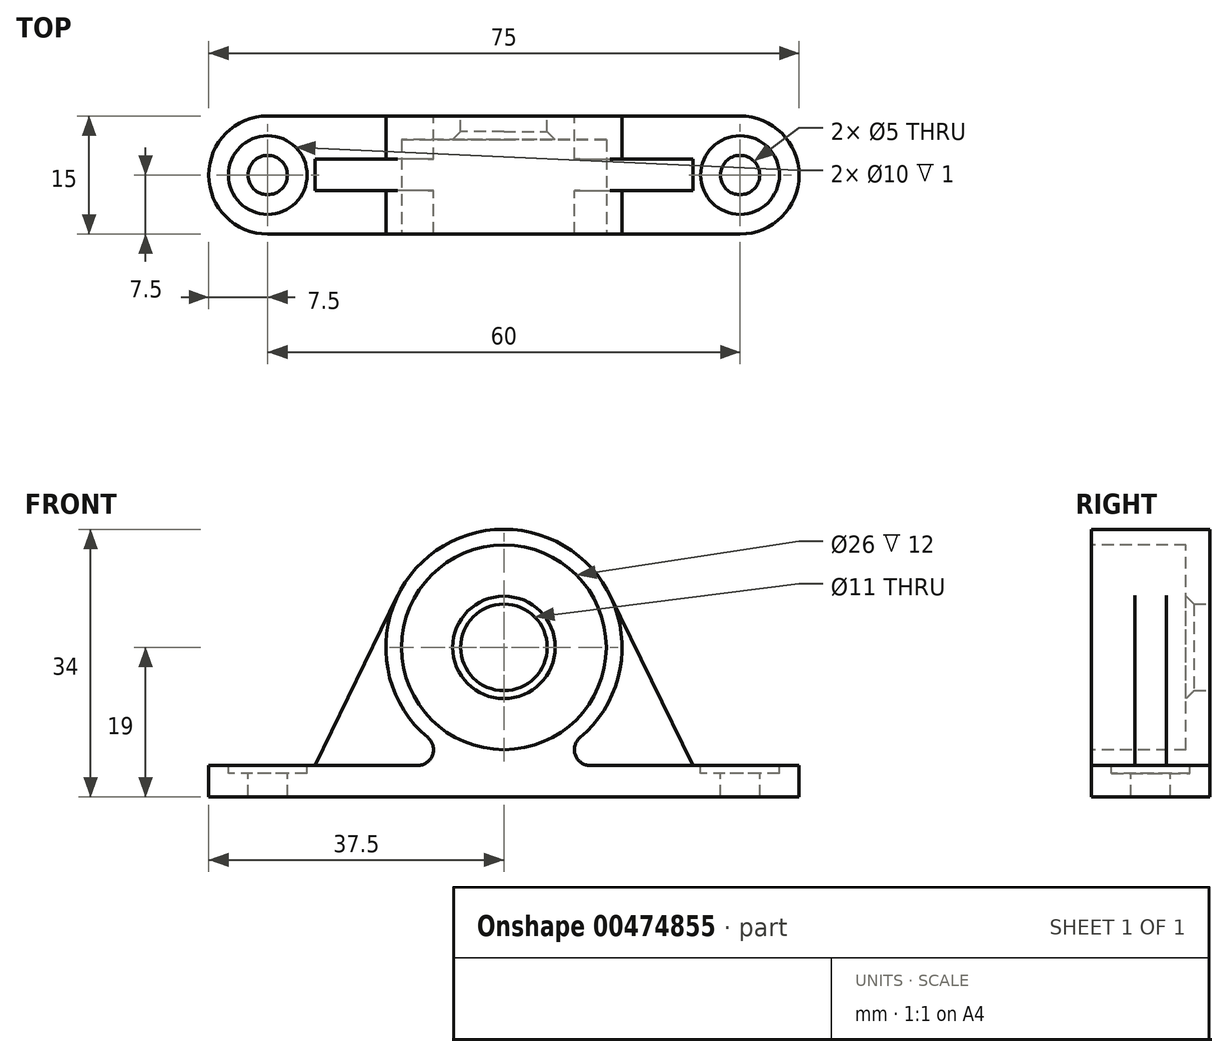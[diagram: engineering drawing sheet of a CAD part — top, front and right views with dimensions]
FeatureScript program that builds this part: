
annotation { "Feature Type Name" : "Feature", "Feature Type Description" : "" }
export const myFeature = defineFeature(function(context is Context, id is Id, definition is map)
    precondition{}
    {
        {
            assignVariable(context, id + "F0", {"name" : "Thickness", "anyValue" : 15});
        }
        {
            var Q0;
            Q0=qCreatedBy(makeId("Front.planeOp"),FACE);
            var sketch = newSketch(context, id + "F1", { "sketchPlane" : qUnion([Q0])});
            skLineSegment(sketch, "E0", {"start": v(0, 0) * mm, "end": v(-37.5, 0) * mm});
            skLineSegment(sketch, "E1", {"start": v(-37.5, 0) * mm, "end": v(-37.5, 4) * mm});
            skLineSegment(sketch, "E2", {"start": v(-37.5, 4) * mm, "end": v(-10.95, 4) * mm});
            skLineSegment(sketch, "E3", {"start": v(0, -14.72) * mm, "end": v(0, 62.74) * mm, "construction": true});
            skArc(sketch, "E4", {"start": v(-9.67, 7.53) * mm, "mid": v(-14.1, 24.14) * mm, "end": v(0, 34) * mm});
            skPoint(sketch, "E5.visualSharp", {"position": v(0, 4) * mm});
            skArc(sketch, "E5.filletArc", {"start": v(-10.95, 4) * mm, "mid": v(-9.08, 5.31) * mm, "end": v(-9.67, 7.53) * mm});
            skLineSegment(sketch, "E6.MirrorCS", {"start": v(37.5, 0) * mm, "end": v(37.5, 4) * mm});
            skLineSegment(sketch, "E7.MirrorCS", {"start": v(37.5, 4) * mm, "end": v(10.95, 4) * mm});
            skLineSegment(sketch, "E8.MirrorCS", {"start": v(0, 0) * mm, "end": v(37.5, 0) * mm});
            skArc(sketch, "E9.MirrorCS", {"start": v(9.67, 7.53) * mm, "mid": v(14.1, 24.14) * mm, "end": v(0, 34) * mm});
            skArc(sketch, "E10.MirrorCS", {"start": v(10.95, 4) * mm, "mid": v(9.08, 5.31) * mm, "end": v(9.67, 7.53) * mm});
            skArc(sketch, "E11", {"start": v(-9.67, 7.53) * mm, "mid": v(0, 4) * mm, "end": v(9.67, 7.53) * mm, "construction": true});
            skSolve(sketch);
        }
        {
            var Q0;
            Q0=qSketchRegion(id+"F1",true);
            extrude(context, id + "F2", {"entities" : qUnion([Q0]), "endBound" : BoundingType.SYMMETRIC, "depth" : 15 * mm});
        }
        {
            var Q0;
            Q0=makeQuery(id+"F2.opExtrude","CAP_FACE",FACE,{"disambiguationData":[OSD([sQuery(id+"F1.wireOp",EDGE,"E0"),sQuery(id+"F1.wireOp",EDGE,"E1"),sQuery(id+"F1.wireOp",EDGE,"E2"),sQuery(id+"F1.wireOp",EDGE,"E5.filletArc"),sQuery(id+"F1.wireOp",EDGE,"E6.MirrorCS"),sQuery(id+"F1.wireOp",EDGE,"E7.MirrorCS"),sQuery(id+"F1.wireOp",EDGE,"E8.MirrorCS"),sQuery(id+"F1.wireOp",EDGE,"E9.MirrorCS"),sQuery(id+"F1.wireOp",EDGE,"E10.MirrorCS"),sQuery(id+"F1.wireOp",EDGE,"E4")])],"isStart":false});
            var sketch = newSketch(context, id + "F3", { "sketchPlane" : qUnion([Q0])});
            skCircle(sketch, "E12", {"center": v(0, 19) * mm, "radius": 13 * mm});
            skSolve(sketch);
        }
        {
            var Q0;
            Q0 = qSketchRegion(id + "F3", true);
            extrude(context, id + "F4", {"entities" : qUnion([Q0]), "operationType" : NewBodyOperationType.REMOVE, "oppositeDirection" : true, "depth" : (getVariable(context, 'Thickness') - 3) * mm});
        }
        {
            var Q0;
            Q0=makeQuery(id+"F2.opExtrude","CAP_FACE",FACE,{"disambiguationData":[OSD([sQuery(id+"F1.wireOp",EDGE,"E0"),sQuery(id+"F1.wireOp",EDGE,"E1"),sQuery(id+"F1.wireOp",EDGE,"E2"),sQuery(id+"F1.wireOp",EDGE,"E5.filletArc"),sQuery(id+"F1.wireOp",EDGE,"E6.MirrorCS"),sQuery(id+"F1.wireOp",EDGE,"E7.MirrorCS"),sQuery(id+"F1.wireOp",EDGE,"E8.MirrorCS"),sQuery(id+"F1.wireOp",EDGE,"E9.MirrorCS"),sQuery(id+"F1.wireOp",EDGE,"E10.MirrorCS"),sQuery(id+"F1.wireOp",EDGE,"E4")])],"isStart":true});
            var sketch = newSketch(context, id + "F5", { "sketchPlane" : qUnion([Q0])});
            skCircle(sketch, "E13", {"center": v(0, 19) * mm, "radius": 5.5 * mm});
            skSolve(sketch);
        }
        {
            var Q0;
            Q0 = qSketchRegion(id + "F5", true);
            extrude(context, id + "F6", {"entities" : qUnion([Q0]), "operationType" : NewBodyOperationType.REMOVE, "endBound" : BoundingType.THROUGH_ALL, "oppositeDirection" : true, "depth" : 25 * mm});
        }
        {
            var Q0;
            Q0=makeQuery(id+"F2.opExtrude","CAP_EDGE",EDGE,{"disambiguationData":[OSD([sQuery(id+"F1.wireOp",EDGE,"E6.MirrorCS")])],"isStart":false});
            var Q1;
            Q1=makeQuery(id+"F2.opExtrude","CAP_EDGE",EDGE,{"disambiguationData":[OSD([sQuery(id+"F1.wireOp",EDGE,"E6.MirrorCS")])],"isStart":true});
            var Q2;
            Q2=makeQuery(id+"F2.opExtrude","CAP_EDGE",EDGE,{"disambiguationData":[OSD([sQuery(id+"F1.wireOp",EDGE,"E1")])],"isStart":false});
            var Q3;
            Q3=makeQuery(id+"F2.opExtrude","CAP_EDGE",EDGE,{"disambiguationData":[OSD([sQuery(id+"F1.wireOp",EDGE,"E1")])],"isStart":true});
            fillet(context, id + "F7", {"entities" : qUnion([Q0, Q1, Q2, Q3]), "radius" : (getVariable(context, 'Thickness') / 2) * mm, "tangentPropagation" : true, "allowEdgeOverflow" : false});
        }
        {
            var Q0;
            Q0=makeQuery(id+"F2.opExtrude","SWEPT_FACE",FACE,{"disambiguationData":[OSD([sQuery(id+"F1.wireOp",EDGE,"E7.MirrorCS")])]});
            var sketch = newSketch(context, id + "F8", { "sketchPlane" : qUnion([Q0])});
            skPoint(sketch, "E14", {"position": v(30, 0) * mm});
            skPoint(sketch, "E15.MirrorP", {"position": v(-30, 0) * mm});
            skSolve(sketch);
        }
        {
            var Q0;
            Q0=sQuery(id+"F8.wireOp",VERTEX,"E14");
            var Q1;
            Q1=sQuery(id+"F8.wireOp",VERTEX,"E15.MirrorP");
            var Q2;
            Q2=makeQuery(id+"F2.opExtrude","SWEPT_BODY",BODY,{"disambiguationData":[OSD([sQuery(id+"F1.wireOp",EDGE,"E0"),sQuery(id+"F1.wireOp",EDGE,"E1"),sQuery(id+"F1.wireOp",EDGE,"E2"),sQuery(id+"F1.wireOp",EDGE,"E5.filletArc"),sQuery(id+"F1.wireOp",EDGE,"E6.MirrorCS"),sQuery(id+"F1.wireOp",EDGE,"E7.MirrorCS"),sQuery(id+"F1.wireOp",EDGE,"E8.MirrorCS"),sQuery(id+"F1.wireOp",EDGE,"E9.MirrorCS"),sQuery(id+"F1.wireOp",EDGE,"E10.MirrorCS"),sQuery(id+"F1.wireOp",EDGE,"E4"),sQuery(id+"F1.wireOp",EDGE,"xOvTdpff-GPNy-Ahw4-pvuq-FGurvRJnDwLL"),sQuery(id+"F1.wireOp",EDGE,"c4084a71-2947-44b7-b196-35892ec3426b0.MirrorCS")])]});
            hole(context, id + "F9", {"style" : HoleStyle.C_BORE, "endStyle" : HoleEndStyle.THROUGH, "holeDiameter" : 5 * mm, "cBoreDiameter" : 10 * mm, "cBoreDepth" : 1 * mm, "isTappedThrough" : true, "tappedDepth" : 12 * mm, "tapClearance" : 3, "locations" : qUnion([Q0, Q1]), "scope" : qUnion([Q2])});
        }
        {
            var Q0;
            Q0=qCreatedBy(makeId("Front.planeOp"),FACE);
            var sketch = newSketch(context, id + "F10", { "sketchPlane" : qUnion([Q0])});
            skLineSegment(sketch, "E16", {"start": v(24, 4) * mm, "end": v(13.48, 25.57) * mm});
            skArc(sketch, "E17.0", {"start": v(9.67, 7.53) * mm, "mid": v(14.68, 15.9) * mm, "end": v(13.48, 25.57) * mm});
            skArc(sketch, "E18.0", {"start": v(10.95, 4) * mm, "mid": v(9.08, 5.31) * mm, "end": v(9.67, 7.53) * mm});
            skPoint(sketch, "E19.0", {"position": v(10.95, 4) * mm});
            skLineSegment(sketch, "E20", {"start": v(10.95, 4) * mm, "end": v(24, 4) * mm});
            skLineSegment(sketch, "E21.0", {"start": v(25, 4) * mm, "end": v(35, 4) * mm, "construction": true});
            skSolve(sketch);
        }
        {
            var Q0;
            {var subQ0=sQuery(id+"F10.wireOp",EDGE,"E16");Q0=makeQuery(id+"F10.imprint","IMPRINT",FACE,{"disambiguationData":[TD([[makeQuery(id+"F10.imprint","IMPRINT",EDGE,{"derivedFrom":subQ0}),1.0]])]});}
            extrude(context, id + "F11", {"entities" : qUnion([Q0]), "endBound" : BoundingType.SYMMETRIC, "depth" : 4 * mm});
        }
        {
            var Q0;
            Q0=makeQuery(id+"F6.boolean.opBoolean","INTERSECT",EDGE,{"derivedFrom":[makeQuery(id+"F4.boolean.opBoolean","COPY",FACE,{"derivedFrom":makeQuery(id+"F4.opExtrude","CAP_FACE",FACE,{"disambiguationData":[OSD([sQuery(id+"F3.wireOp",EDGE,"E12")])],"isStart":false})}),makeQuery(id+"F6.opExtrude","SWEPT_FACE",FACE,{"disambiguationData":[OSD([sQuery(id+"F5.wireOp",EDGE,"E13")])]})]});
            chamfer(context, id + "F12", {"entities" : qUnion([Q0]), "width" : 1 * mm, "tangentPropagation" : true});
        }
        {
            var Q0;
            Q0=makeQuery(id+"F11.opExtrude","SWEPT_BODY",BODY,{"disambiguationData":[OSD([sQuery(id+"F10.wireOp",EDGE,"E16"),sQuery(id+"F10.wireOp",EDGE,"E17.0"),sQuery(id+"F10.wireOp",EDGE,"E18.0"),sQuery(id+"F10.wireOp",EDGE,"d5b68f82-8350-41d3-9ff2-1b9ca3f2bff8.0")])]});
            var Q1;
            Q1=qCreatedBy(makeId("Right.planeOp"),FACE);
            mirror(context, id + "F13", {"operationType" : NewBodyOperationType.ADD, "entities" : qUnion([Q0]), "mirrorPlane" : qUnion([Q1])});
        }
    });
